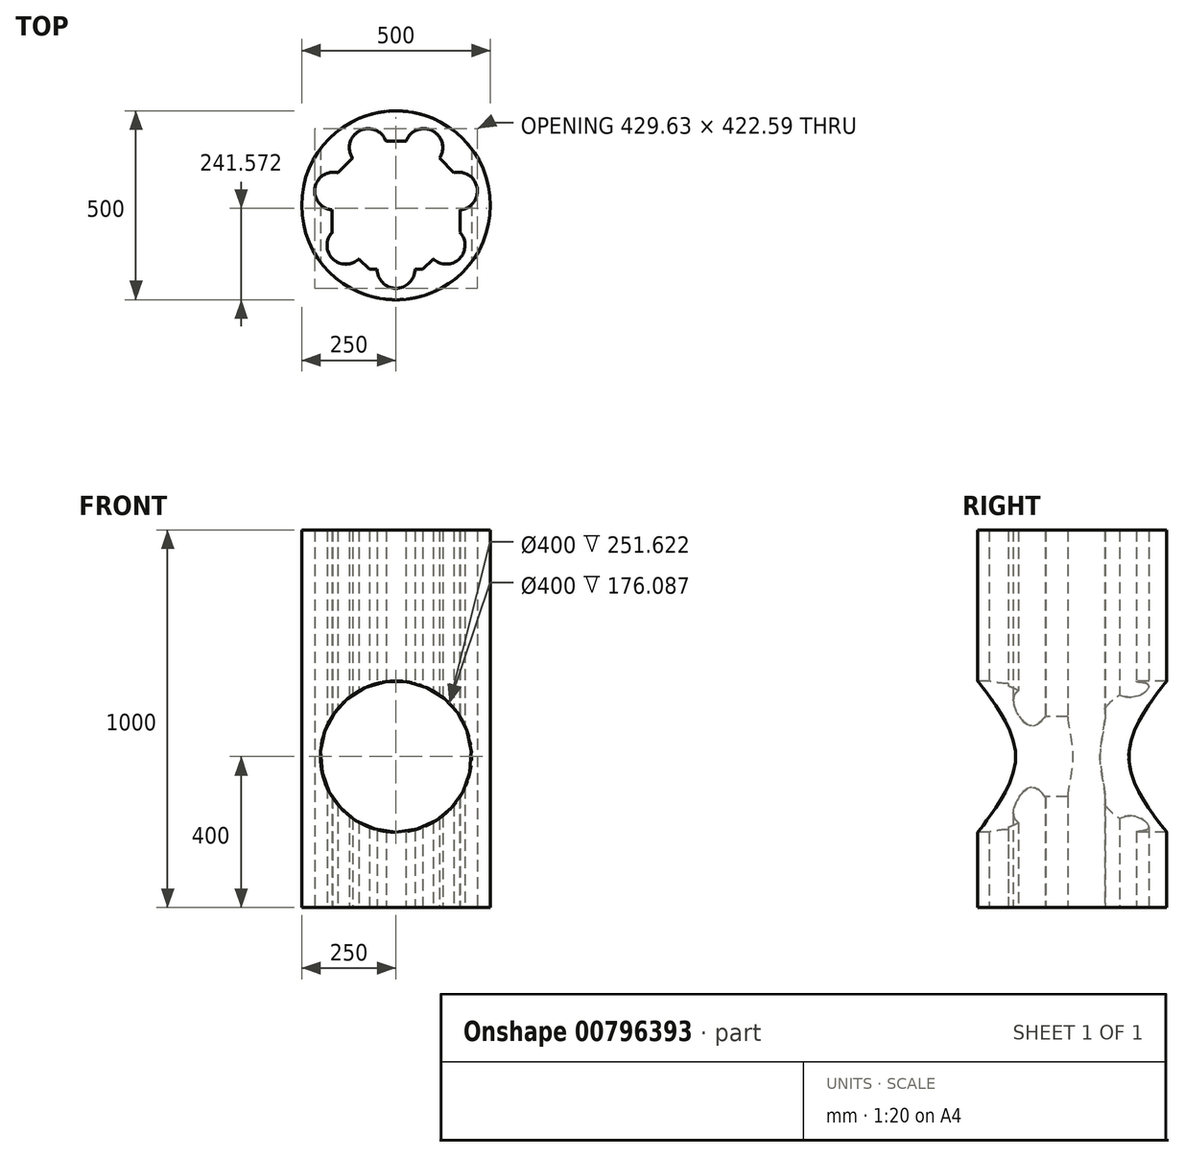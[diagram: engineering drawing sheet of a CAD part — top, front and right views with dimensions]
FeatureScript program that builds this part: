
annotation { "Feature Type Name" : "Feature", "Feature Type Description" : "" }
export const myFeature = defineFeature(function(context is Context, id is Id, definition is map)
    precondition{}
    {
        {
            var Q0;
            Q0=qCreatedBy(makeId("Top.planeOp"),FACE);
            var sketch = newSketch(context, id + "F0", { "sketchPlane" : qUnion([Q0])});
            skCircle(sketch, "E0", {"center": v(0, 0) * mm, "radius": 250 * mm});
            skArc(sketch, "E1.cCircle", {"start": v(0, 183.7) * mm, "mid": v(-35.84, 180.18) * mm, "end": v(-70.3, 169.72) * mm, "construction": true});
            skLineSegment(sketch, "E1.0", {"start": v(70.3, 169.72) * mm, "end": v(169.72, 70.3) * mm});
            skLineSegment(sketch, "E1.1", {"start": v(169.72, 70.3) * mm, "end": v(169.72, -70.3) * mm});
            skLineSegment(sketch, "E1.2", {"start": v(169.72, -70.3) * mm, "end": v(70.3, -169.72) * mm});
            skLineSegment(sketch, "E1.3", {"start": v(70.3, -169.72) * mm, "end": v(-70.3, -169.72) * mm});
            skLineSegment(sketch, "E1.4", {"start": v(-70.3, -169.72) * mm, "end": v(-169.72, -70.3) * mm});
            skLineSegment(sketch, "E1.5", {"start": v(-169.72, -70.3) * mm, "end": v(-169.72, 70.3) * mm});
            skLineSegment(sketch, "E1.6", {"start": v(-169.72, 70.3) * mm, "end": v(-70.3, 169.72) * mm});
            skLineSegment(sketch, "E1.7", {"start": v(-70.3, 169.72) * mm, "end": v(70.3, 169.72) * mm});
            skSolve(sketch);
        }
        {
            var Q0;
            Q0 = qSketchRegion(id + "F0", true);
            extrude(context, id + "F1", {"entities" : qUnion([Q0]), "depth" : 1000 * mm, "offsetDistance" : 25.4 * mm});
        }
        {
            var Q0;
            Q0=qCreatedBy(makeId("Front.planeOp"),FACE);
            var sketch = newSketch(context, id + "F2", { "sketchPlane" : qUnion([Q0])});
            skCircle(sketch, "E2", {"center": v(0, 400) * mm, "radius": 200 * mm});
            skSolve(sketch);
        }
        {
            var Q0;
            Q0=makeQuery(id+"F2.imprint","IMPRINT",FACE,{"disambiguationData":[TD([[makeQuery(id+"F2.imprint","IMPRINT",EDGE,{"derivedFrom":sQuery(id+"F2.wireOp",EDGE,"E2")}),1.0]])]});
            var Q1;
            Q1=sQuery(id+"F2.wireOp",EDGE,"E2");
            extrude(context, id + "F3", {"entities" : qUnion([Q0]), "operationType" : NewBodyOperationType.REMOVE, "surfaceEntities" : qUnion([Q1]), "oppositeDirection" : true, "depth" : 360.06 * mm, "offsetDistance" : 25.4 * mm, "hasSecondDirection" : true, "secondDirectionOppositeDirection" : false, "secondDirectionDepth" : 472.48 * mm});
        }
        {
            var Q0;
            Q0=makeQuery(id+"F1.opExtrude","CAP_FACE",FACE,{"disambiguationData":[OSD([sQuery(id+"F0.wireOp",EDGE,"E0"),sQuery(id+"F0.wireOp",EDGE,"E1.0"),sQuery(id+"F0.wireOp",EDGE,"E1.1"),sQuery(id+"F0.wireOp",EDGE,"E1.2"),sQuery(id+"F0.wireOp",EDGE,"E1.3"),sQuery(id+"F0.wireOp",EDGE,"E1.4"),sQuery(id+"F0.wireOp",EDGE,"E1.5"),sQuery(id+"F0.wireOp",EDGE,"E1.6"),sQuery(id+"F0.wireOp",EDGE,"E1.7")])],"isStart":true});
            var sketch = newSketch(context, id + "F4", { "sketchPlane" : qUnion([Q0])});
            skCircle(sketch, "E3", {"center": v(0, 169.72) * mm, "radius": 50 * mm});
            skCircle(sketch, "E4.1.0", {"center": v(-132.7, 105.82) * mm, "radius": 50 * mm});
            skCircle(sketch, "E4.2.0", {"center": v(-165.47, -37.77) * mm, "radius": 50 * mm});
            skCircle(sketch, "E4.3.0", {"center": v(-73.64, -152.92) * mm, "radius": 50 * mm});
            skCircle(sketch, "E4.4.0", {"center": v(73.64, -152.92) * mm, "radius": 50 * mm});
            skCircle(sketch, "E4.5.0", {"center": v(165.47, -37.77) * mm, "radius": 50 * mm});
            skCircle(sketch, "E4.6.0", {"center": v(132.7, 105.82) * mm, "radius": 50 * mm});
            skPoint(sketch, "E4.center", {"position": v(0, 0) * mm});
            skSolve(sketch);
        }
        {
            var Q0;
            {var subQ0=sQuery(id+"F4.wireOp",EDGE,"E4.1.0");var subQ1=makeQuery(id+"F1.opExtrude","CAP_EDGE",EDGE,{"disambiguationData":[OSD([sQuery(id+"F0.wireOp",EDGE,"E1.4")])],"isStart":true});var subQ2=makeQuery(id+"F4.imprint","INTERSECT",VERTEX,{"disambiguationData":[OD(0.0)],"derivedFrom":[subQ1,subQ0]});Q0=makeQuery(id+"F4.imprint","IMPRINT",FACE,{"disambiguationData":[TD([[makeQuery(id+"F4.imprint","IMPRINT",EDGE,{"disambiguationData":[TD([[subQ2,-1.0]])],"derivedFrom":subQ0}),1.0]])]});}
            var Q1;
            {var subQ0=sQuery(id+"F4.wireOp",EDGE,"E4.1.0");var subQ1=makeQuery(id+"F1.opExtrude","CAP_EDGE",EDGE,{"disambiguationData":[OSD([sQuery(id+"F0.wireOp",EDGE,"E1.4")])],"isStart":true});var subQ2=makeQuery(id+"F4.imprint","INTERSECT",VERTEX,{"disambiguationData":[OD(0.0)],"derivedFrom":[subQ1,subQ0]});Q1=makeQuery(id+"F4.imprint","IMPRINT",FACE,{"disambiguationData":[TD([[makeQuery(id+"F4.imprint","IMPRINT",EDGE,{"disambiguationData":[TD([[subQ2,1.0]])],"derivedFrom":subQ0}),1.0]])]});}
            var Q2;
            {var subQ0=sQuery(id+"F4.wireOp",EDGE,"E3");var subQ1=makeQuery(id+"F1.opExtrude","CAP_EDGE",EDGE,{"disambiguationData":[OSD([sQuery(id+"F0.wireOp",EDGE,"E1.3")])],"isStart":true});var subQ2=makeQuery(id+"F4.imprint","INTERSECT",VERTEX,{"disambiguationData":[OD(0.0)],"derivedFrom":[subQ1,subQ0]});Q2=makeQuery(id+"F4.imprint","IMPRINT",FACE,{"disambiguationData":[TD([[makeQuery(id+"F4.imprint","IMPRINT",EDGE,{"disambiguationData":[TD([[subQ2,-1.0]])],"derivedFrom":subQ0}),1.0]])]});}
            var Q3;
            {var subQ0=sQuery(id+"F4.wireOp",EDGE,"E3");var subQ1=makeQuery(id+"F1.opExtrude","CAP_EDGE",EDGE,{"disambiguationData":[OSD([sQuery(id+"F0.wireOp",EDGE,"E1.3")])],"isStart":true});var subQ2=makeQuery(id+"F4.imprint","INTERSECT",VERTEX,{"disambiguationData":[OD(0.0)],"derivedFrom":[subQ1,subQ0]});Q3=makeQuery(id+"F4.imprint","IMPRINT",FACE,{"disambiguationData":[TD([[makeQuery(id+"F4.imprint","IMPRINT",EDGE,{"disambiguationData":[TD([[subQ2,1.0]])],"derivedFrom":subQ0}),1.0]])]});}
            var Q4;
            {var subQ0=sQuery(id+"F4.wireOp",EDGE,"E4.6.0");var subQ1=makeQuery(id+"F1.opExtrude","CAP_EDGE",EDGE,{"disambiguationData":[OSD([sQuery(id+"F0.wireOp",EDGE,"E1.2")])],"isStart":true});var subQ2=makeQuery(id+"F4.imprint","INTERSECT",VERTEX,{"disambiguationData":[OD(0.0)],"derivedFrom":[subQ1,subQ0]});Q4=makeQuery(id+"F4.imprint","IMPRINT",FACE,{"disambiguationData":[TD([[makeQuery(id+"F4.imprint","IMPRINT",EDGE,{"disambiguationData":[TD([[subQ2,1.0]])],"derivedFrom":subQ0}),1.0]])]});}
            var Q5;
            {var subQ0=sQuery(id+"F4.wireOp",EDGE,"E4.6.0");var subQ1=makeQuery(id+"F1.opExtrude","CAP_EDGE",EDGE,{"disambiguationData":[OSD([sQuery(id+"F0.wireOp",EDGE,"E1.2")])],"isStart":true});var subQ2=makeQuery(id+"F4.imprint","INTERSECT",VERTEX,{"disambiguationData":[OD(0.0)],"derivedFrom":[subQ1,subQ0]});Q5=makeQuery(id+"F4.imprint","IMPRINT",FACE,{"disambiguationData":[TD([[makeQuery(id+"F4.imprint","IMPRINT",EDGE,{"disambiguationData":[TD([[subQ2,-1.0]])],"derivedFrom":subQ0}),1.0]])]});}
            var Q6;
            {var subQ0=sQuery(id+"F4.wireOp",EDGE,"E4.2.0");var subQ1=makeQuery(id+"F1.opExtrude","CAP_EDGE",EDGE,{"disambiguationData":[OSD([sQuery(id+"F0.wireOp",EDGE,"E1.5")])],"isStart":true});var subQ2=makeQuery(id+"F4.imprint","INTERSECT",VERTEX,{"derivedFrom":[subQ1,subQ0]});Q6=makeQuery(id+"F4.imprint","IMPRINT",FACE,{"disambiguationData":[TD([[makeQuery(id+"F4.imprint","IMPRINT",EDGE,{"disambiguationData":[TD([[subQ2,1.0]])],"derivedFrom":subQ0}),1.0]])]});}
            var Q7;
            {var subQ0=sQuery(id+"F4.wireOp",EDGE,"E4.2.0");var subQ1=makeQuery(id+"F1.opExtrude","CAP_EDGE",EDGE,{"disambiguationData":[OSD([sQuery(id+"F0.wireOp",EDGE,"E1.5")])],"isStart":true});var subQ2=makeQuery(id+"F4.imprint","INTERSECT",VERTEX,{"derivedFrom":[subQ1,subQ0]});Q7=makeQuery(id+"F4.imprint","IMPRINT",FACE,{"disambiguationData":[TD([[makeQuery(id+"F4.imprint","IMPRINT",EDGE,{"disambiguationData":[TD([[subQ2,-1.0]])],"derivedFrom":subQ0}),1.0]])]});}
            var Q8;
            {var subQ0=sQuery(id+"F4.wireOp",EDGE,"E4.5.0");var subQ1=makeQuery(id+"F1.opExtrude","CAP_EDGE",EDGE,{"disambiguationData":[OSD([sQuery(id+"F0.wireOp",EDGE,"E1.0")])],"isStart":true});var subQ2=makeQuery(id+"F4.imprint","INTERSECT",VERTEX,{"derivedFrom":[subQ1,subQ0]});Q8=makeQuery(id+"F4.imprint","IMPRINT",FACE,{"disambiguationData":[TD([[makeQuery(id+"F4.imprint","IMPRINT",EDGE,{"disambiguationData":[TD([[subQ2,-1.0]])],"derivedFrom":subQ0}),1.0]])]});}
            var Q9;
            {var subQ0=sQuery(id+"F4.wireOp",EDGE,"E4.5.0");var subQ1=makeQuery(id+"F1.opExtrude","CAP_EDGE",EDGE,{"disambiguationData":[OSD([sQuery(id+"F0.wireOp",EDGE,"E1.0")])],"isStart":true});var subQ2=makeQuery(id+"F4.imprint","INTERSECT",VERTEX,{"derivedFrom":[subQ1,subQ0]});Q9=makeQuery(id+"F4.imprint","IMPRINT",FACE,{"disambiguationData":[TD([[makeQuery(id+"F4.imprint","IMPRINT",EDGE,{"disambiguationData":[TD([[subQ2,1.0]])],"derivedFrom":subQ0}),1.0]])]});}
            var Q10;
            {var subQ0=sQuery(id+"F4.wireOp",EDGE,"E4.4.0");var subQ1=makeQuery(id+"F1.opExtrude","CAP_EDGE",EDGE,{"disambiguationData":[OSD([sQuery(id+"F0.wireOp",EDGE,"E1.0")])],"isStart":true});var subQ2=makeQuery(id+"F4.imprint","INTERSECT",VERTEX,{"derivedFrom":[subQ1,subQ0]});Q10=makeQuery(id+"F4.imprint","IMPRINT",FACE,{"disambiguationData":[TD([[makeQuery(id+"F4.imprint","IMPRINT",EDGE,{"disambiguationData":[TD([[subQ2,-1.0]])],"derivedFrom":subQ0}),1.0]])]});}
            var Q11;
            {var subQ0=sQuery(id+"F4.wireOp",EDGE,"E4.4.0");var subQ1=makeQuery(id+"F1.opExtrude","CAP_EDGE",EDGE,{"disambiguationData":[OSD([sQuery(id+"F0.wireOp",EDGE,"E1.0")])],"isStart":true});var subQ2=makeQuery(id+"F4.imprint","INTERSECT",VERTEX,{"derivedFrom":[subQ1,subQ0]});Q11=makeQuery(id+"F4.imprint","IMPRINT",FACE,{"disambiguationData":[TD([[makeQuery(id+"F4.imprint","IMPRINT",EDGE,{"disambiguationData":[TD([[subQ2,1.0]])],"derivedFrom":subQ0}),1.0]])]});}
            var Q12;
            {var subQ0=sQuery(id+"F4.wireOp",EDGE,"E4.3.0");var subQ1=makeQuery(id+"F1.opExtrude","CAP_EDGE",EDGE,{"disambiguationData":[OSD([sQuery(id+"F0.wireOp",EDGE,"E1.6")])],"isStart":true});var subQ2=makeQuery(id+"F4.imprint","INTERSECT",VERTEX,{"derivedFrom":[subQ1,subQ0]});Q12=makeQuery(id+"F4.imprint","IMPRINT",FACE,{"disambiguationData":[TD([[makeQuery(id+"F4.imprint","IMPRINT",EDGE,{"disambiguationData":[TD([[subQ2,1.0]])],"derivedFrom":subQ0}),1.0]])]});}
            var Q13;
            {var subQ0=sQuery(id+"F4.wireOp",EDGE,"E4.3.0");var subQ1=makeQuery(id+"F1.opExtrude","CAP_EDGE",EDGE,{"disambiguationData":[OSD([sQuery(id+"F0.wireOp",EDGE,"E1.6")])],"isStart":true});var subQ2=makeQuery(id+"F4.imprint","INTERSECT",VERTEX,{"derivedFrom":[subQ1,subQ0]});Q13=makeQuery(id+"F4.imprint","IMPRINT",FACE,{"disambiguationData":[TD([[makeQuery(id+"F4.imprint","IMPRINT",EDGE,{"disambiguationData":[TD([[subQ2,-1.0]])],"derivedFrom":subQ0}),1.0]])]});}
            extrude(context, id + "F5", {"entities" : qUnion([Q0, Q1, Q2, Q3, Q4, Q5, Q6, Q7, Q8, Q9, Q10, Q11, Q12, Q13]), "operationType" : NewBodyOperationType.REMOVE, "endBound" : BoundingType.THROUGH_ALL, "oppositeDirection" : true, "depth" : 25.4 * mm, "offsetDistance" : 25.4 * mm});
        }
    });
